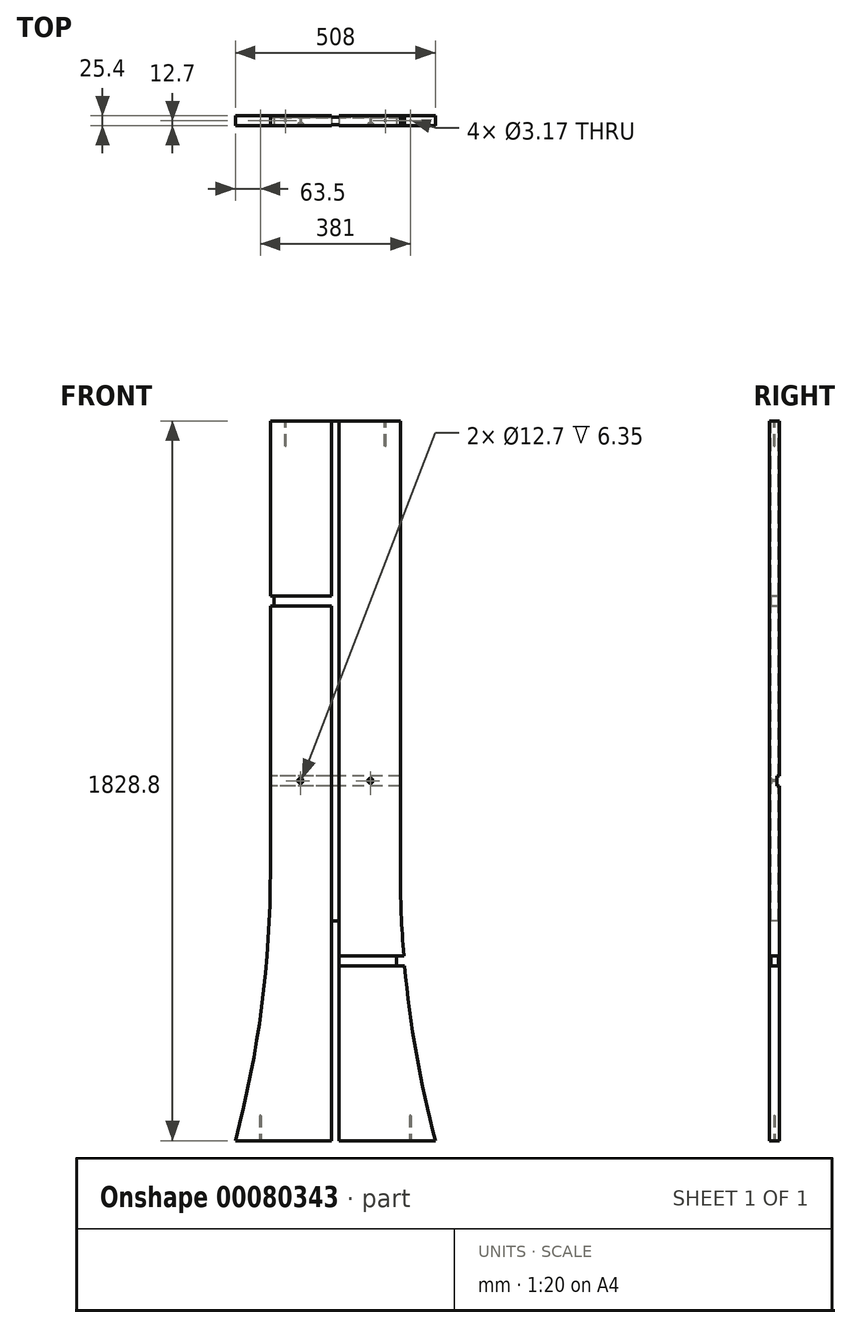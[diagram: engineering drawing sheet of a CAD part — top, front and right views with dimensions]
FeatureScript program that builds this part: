
annotation { "Feature Type Name" : "Feature", "Feature Type Description" : "" }
export const myFeature = defineFeature(function(context is Context, id is Id, definition is map)
    precondition{}
    {
        {
            var Q0;
            Q0=qCreatedBy(makeId("Front.planeOp"),FACE);
            var sketch = newSketch(context, id + "F0", { "sketchPlane" : qUnion([Q0])});
            skLineSegment(sketch, "E0", {"start": v(0, 0) * mm, "end": v(0, 1828.8) * mm, "construction": true});
            skLineSegment(sketch, "E1", {"start": v(0, 1828.8) * mm, "end": v(-165.1, 1828.8) * mm});
            skLineSegment(sketch, "E2", {"start": v(0, 0) * mm, "end": v(-254, 0) * mm});
            skLineSegment(sketch, "E3", {"start": v(-165.1, 1828.8) * mm, "end": v(-165.1, 685.8) * mm});
            skArc(sketch, "E4", {"start": v(-254, 0) * mm, "mid": v(-187.42, 340.03) * mm, "end": v(-165.1, 685.8) * mm});
            skLineSegment(sketch, "E5.MirrorCS", {"start": v(0, 1828.8) * mm, "end": v(165.1, 1828.8) * mm});
            skLineSegment(sketch, "E6.MirrorCS", {"start": v(165.1, 1828.8) * mm, "end": v(165.1, 685.8) * mm});
            skArc(sketch, "E7.MirrorCS", {"start": v(254, 0) * mm, "mid": v(187.42, 340.03) * mm, "end": v(165.1, 685.8) * mm});
            skLineSegment(sketch, "E8.MirrorCS", {"start": v(0, 0) * mm, "end": v(254, 0) * mm});
            skSolve(sketch);
        }
        {
            var Q0;
            Q0=makeQuery(id+"F0.imprint","IMPRINT",FACE,{"disambiguationData":[TD([[makeQuery(id+"F0.imprint","IMPRINT",EDGE,{"derivedFrom":sQuery(id+"F0.wireOp",EDGE,"E1")}),1.0]])]});
            extrude(context, id + "F1", {"entities" : qUnion([Q0]), "endBound" : BoundingType.SYMMETRIC, "depth" : 25.4 * mm});
        }
        {
            var Q0;
            Q0=makeQuery(id+"F1.opExtrude","CAP_FACE",FACE,{"disambiguationData":[OSD([sQuery(id+"F0.wireOp",EDGE,"E1"),sQuery(id+"F0.wireOp",EDGE,"E2"),sQuery(id+"F0.wireOp",EDGE,"E3"),sQuery(id+"F0.wireOp",EDGE,"E4"),sQuery(id+"F0.wireOp",EDGE,"E6.MirrorCS"),sQuery(id+"F0.wireOp",EDGE,"E5.MirrorCS"),sQuery(id+"F0.wireOp",EDGE,"E7.MirrorCS"),sQuery(id+"F0.wireOp",EDGE,"E8.MirrorCS")])],"isStart":false});
            var sketch = newSketch(context, id + "F28", { "sketchPlane" : qUnion([Q0])});
            skLineSegment(sketch, "E9.bottom", {"start": v(9.53, 0) * mm, "end": v(-9.52, 0) * mm});
            skLineSegment(sketch, "E9.top", {"start": v(9.53, 558.8) * mm, "end": v(-9.53, 558.8) * mm});
            skLineSegment(sketch, "E9.left", {"start": v(9.53, 0) * mm, "end": v(9.53, 558.8) * mm});
            skLineSegment(sketch, "E9.right", {"start": v(-9.52, 0) * mm, "end": v(-9.53, 558.8) * mm});
            skSolve(sketch);
        }
        {
            var Q0;
            Q0=qSketchRegion(id+"F28",true);
            extrude(context, id + "F29", {"entities" : qUnion([Q0]), "operationType" : NewBodyOperationType.REMOVE, "oppositeDirection" : true, "depth" : 25.4 * mm});
        }
        {
            var Q0;
            Q0=makeQuery(id+"F28.imprint","IMPRINT",FACE,{"disambiguationData":[TD([[makeQuery(id+"F28.imprint","IMPRINT",EDGE,{"derivedFrom":sQuery(id+"F28.wireOp",EDGE,"E9.top")}),-1.0]])]});
            var sketch = newSketch(context, id + "F2", { "sketchPlane" : qUnion([Q0])});
            skPoint(sketch, "E10", {"position": v(-88.9, 914.4) * mm});
            skPoint(sketch, "E11", {"position": v(88.9, 914.4) * mm});
            skSolve(sketch);
        }
        {
            var Q0;
            Q0=sQuery(id+"F2.wireOp",VERTEX,"E10");
            var Q1;
            Q1=sQuery(id+"F2.wireOp",VERTEX,"E11");
            var Q2;
            Q2=makeQuery(id+"F1.opExtrude","SWEPT_BODY",BODY,{"disambiguationData":[OSD([sQuery(id+"F0.wireOp",EDGE,"E1"),sQuery(id+"F0.wireOp",EDGE,"E2"),sQuery(id+"F0.wireOp",EDGE,"E3"),sQuery(id+"F0.wireOp",EDGE,"E4"),sQuery(id+"F0.wireOp",EDGE,"E6.MirrorCS"),sQuery(id+"F0.wireOp",EDGE,"E5.MirrorCS"),sQuery(id+"F0.wireOp",EDGE,"E7.MirrorCS"),sQuery(id+"F0.wireOp",EDGE,"E8.MirrorCS")])]});
            hole(context, id + "F3", {"style" : HoleStyle.C_BORE, "endStyle" : HoleEndStyle.BLIND, "holeDiameter" : 3.17 * mm, "cBoreDiameter" : 12.7 * mm, "cBoreDepth" : 6.35 * mm, "holeDepth" : 63.5 * mm, "locations" : qUnion([Q0, Q1]), "scope" : qUnion([Q2])});
        }
        {
            var Q0;
            Q0=makeQuery(id+"F1.opExtrude","SWEPT_FACE",FACE,{"disambiguationData":[OSD([sQuery(id+"F0.wireOp",EDGE,"E1"),sQuery(id+"F0.wireOp",EDGE,"E5.MirrorCS")])]});
            var sketch = newSketch(context, id + "F4", { "sketchPlane" : qUnion([Q0])});
            skPoint(sketch, "E12", {"position": v(-127, 0) * mm});
            skPoint(sketch, "E13", {"position": v(127, 0) * mm});
            skSolve(sketch);
        }
        {
            var Q0;
            Q0=sQuery(id+"F4.wireOp",VERTEX,"E12");
            var Q1;
            Q1=sQuery(id+"F4.wireOp",VERTEX,"E13");
            var Q2;
            Q2=makeQuery(id+"F1.opExtrude","SWEPT_BODY",BODY,{"disambiguationData":[OSD([sQuery(id+"F0.wireOp",EDGE,"E1"),sQuery(id+"F0.wireOp",EDGE,"E2"),sQuery(id+"F0.wireOp",EDGE,"E3"),sQuery(id+"F0.wireOp",EDGE,"E4"),sQuery(id+"F0.wireOp",EDGE,"E6.MirrorCS"),sQuery(id+"F0.wireOp",EDGE,"E5.MirrorCS"),sQuery(id+"F0.wireOp",EDGE,"E7.MirrorCS"),sQuery(id+"F0.wireOp",EDGE,"E8.MirrorCS")])]});
            hole(context, id + "F5", {"style" : HoleStyle.SIMPLE, "endStyle" : HoleEndStyle.BLIND, "holeDiameter" : 3.17 * mm, "holeDepth" : 63.5 * mm, "locations" : qUnion([Q0, Q1]), "scope" : qUnion([Q2])});
        }
        {
            var Q0;
            {var subQ0=sQuery(id+"F0.wireOp",EDGE,"E8.MirrorCS");var subQ4=sQuery(id+"F0.wireOp",EDGE,"E4");var subQ6=sQuery(id+"F0.wireOp",EDGE,"E2");Q0=makeQuery(id+"F29.boolean.opBoolean","SPLIT",FACE,{"disambiguationData":[TD([makeQuery(id+"F1.opExtrude","SWEPT_FACE",FACE,{"disambiguationData":[OSD([subQ4])]})])],"derivedFrom":makeQuery(id+"F1.opExtrude","SWEPT_FACE",FACE,{"disambiguationData":[OSD([subQ6,subQ0])]})});}
            var sketch = newSketch(context, id + "F6", { "sketchPlane" : qUnion([Q0])});
            skPoint(sketch, "E14", {"position": v(-190.5, 0) * mm});
            skPoint(sketch, "E15", {"position": v(190.5, 0) * mm});
            skSolve(sketch);
        }
        {
            var Q0;
            Q0=sQuery(id+"F6.wireOp",VERTEX,"E14");
            var Q1;
            Q1=sQuery(id+"F6.wireOp",VERTEX,"E15");
            var Q2;
            Q2=makeQuery(id+"F1.opExtrude","SWEPT_BODY",BODY,{"disambiguationData":[OSD([sQuery(id+"F0.wireOp",EDGE,"E1"),sQuery(id+"F0.wireOp",EDGE,"E2"),sQuery(id+"F0.wireOp",EDGE,"E3"),sQuery(id+"F0.wireOp",EDGE,"E4"),sQuery(id+"F0.wireOp",EDGE,"E6.MirrorCS"),sQuery(id+"F0.wireOp",EDGE,"E5.MirrorCS"),sQuery(id+"F0.wireOp",EDGE,"E7.MirrorCS"),sQuery(id+"F0.wireOp",EDGE,"E8.MirrorCS")])]});
            hole(context, id + "F7", {"style" : HoleStyle.SIMPLE, "endStyle" : HoleEndStyle.BLIND, "holeDiameter" : 3.17 * mm, "holeDepth" : 63.5 * mm, "locations" : qUnion([Q0, Q1]), "scope" : qUnion([Q2])});
        }
        {
            var Q0;
            Q0=makeQuery(id+"F1.opExtrude","CAP_FACE",FACE,{"disambiguationData":[OSD([sQuery(id+"F0.wireOp",EDGE,"E1"),sQuery(id+"F0.wireOp",EDGE,"E2"),sQuery(id+"F0.wireOp",EDGE,"E3"),sQuery(id+"F0.wireOp",EDGE,"E4"),sQuery(id+"F0.wireOp",EDGE,"E6.MirrorCS"),sQuery(id+"F0.wireOp",EDGE,"E5.MirrorCS"),sQuery(id+"F0.wireOp",EDGE,"E7.MirrorCS"),sQuery(id+"F0.wireOp",EDGE,"E8.MirrorCS")])],"isStart":true});
            var sketch = newSketch(context, id + "F8", { "sketchPlane" : qUnion([Q0])});
            skLineSegment(sketch, "E16", {"start": v(-88.9, 914.4) * mm, "end": v(88.9, 914.4) * mm, "construction": true});
            skLineSegment(sketch, "E17", {"start": v(88.9, 914.4) * mm, "end": v(165.1, 914.4) * mm, "construction": true});
            skLineSegment(sketch, "E18", {"start": v(-88.9, 914.4) * mm, "end": v(-165.1, 914.4) * mm, "construction": true});
            skLineSegment(sketch, "E19.bottom", {"start": v(-165.1, 927.1) * mm, "end": v(165.1, 927.1) * mm});
            skLineSegment(sketch, "E19.top", {"start": v(-165.1, 901.7) * mm, "end": v(165.1, 901.7) * mm});
            skLineSegment(sketch, "E19.left", {"start": v(-165.1, 927.1) * mm, "end": v(-165.1, 901.7) * mm});
            skLineSegment(sketch, "E19.right", {"start": v(165.1, 927.1) * mm, "end": v(165.1, 901.7) * mm});
            skPoint(sketch, "E19.middle", {"position": v(0, 914.4) * mm});
            skSolve(sketch);
        }
        {
            var Q0;
            Q0 = qSketchRegion(id + "F8", true);
            extrude(context, id + "F9", {"entities" : qUnion([Q0]), "operationType" : NewBodyOperationType.REMOVE, "oppositeDirection" : true, "depth" : 6.35 * mm});
        }
        {
            var Q0;
            Q0=makeQuery(id+"F28.imprint","IMPRINT",FACE,{"disambiguationData":[TD([[makeQuery(id+"F28.imprint","IMPRINT",EDGE,{"derivedFrom":sQuery(id+"F28.wireOp",EDGE,"E9.top")}),-1.0]])]});
            var sketch = newSketch(context, id + "F10", { "sketchPlane" : qUnion([Q0])});
            skLineSegment(sketch, "E20", {"start": v(0, 0) * mm, "end": v(0, 558.8) * mm, "construction": true});
            skLineSegment(sketch, "E21", {"start": v(0, 558.8) * mm, "end": v(-9.52, 558.8) * mm, "construction": true});
            skLineSegment(sketch, "E22", {"start": v(0, 558.8) * mm, "end": v(9.52, 558.8) * mm, "construction": true});
            skLineSegment(sketch, "E23.bottom", {"start": v(-9.52, 558.8) * mm, "end": v(9.52, 558.8) * mm});
            skLineSegment(sketch, "E23.top", {"start": v(-9.53, 1828.8) * mm, "end": v(9.52, 1828.8) * mm});
            skLineSegment(sketch, "E23.left", {"start": v(-9.52, 558.8) * mm, "end": v(-9.52, 1828.8) * mm});
            skLineSegment(sketch, "E23.right", {"start": v(9.52, 558.8) * mm, "end": v(9.52, 1828.8) * mm});
            skSolve(sketch);
        }
        {
            var Q0;
            Q0 = qSketchRegion(id + "F10", true);
            extrude(context, id + "F11", {"entities" : qUnion([Q0]), "operationType" : NewBodyOperationType.REMOVE, "oppositeDirection" : true, "depth" : 3.17 * mm});
        }
        {
            var Q0;
            {var subQ0=sQuery(id+"F0.wireOp",EDGE,"E6.MirrorCS");var subQ1=sQuery(id+"F0.wireOp",EDGE,"E4");var subQ2=sQuery(id+"F0.wireOp",EDGE,"E3");var subQ3=sQuery(id+"F0.wireOp",EDGE,"E8.MirrorCS");var subQ4=sQuery(id+"F0.wireOp",EDGE,"E2");var subQ5=sQuery(id+"F0.wireOp",EDGE,"E7.MirrorCS");Q0=makeQuery(id+"F9.boolean.opBoolean","SPLIT",FACE,{"disambiguationData":[TD([makeQuery(id+"F1.opExtrude","SWEPT_FACE",FACE,{"disambiguationData":[OSD([subQ1])]})])],"derivedFrom":makeQuery(id+"F1.opExtrude","CAP_FACE",FACE,{"disambiguationData":[OSD([sQuery(id+"F0.wireOp",EDGE,"E1"),subQ4,subQ2,subQ1,subQ0,sQuery(id+"F0.wireOp",EDGE,"E5.MirrorCS"),subQ5,subQ3])],"isStart":true})});}
            var sketch = newSketch(context, id + "F12", { "sketchPlane" : qUnion([Q0])});
            skLineSegment(sketch, "E24.bottom", {"start": v(-9.53, 558.8) * mm, "end": v(9.53, 558.8) * mm});
            skLineSegment(sketch, "E24.top", {"start": v(-9.53, 901.7) * mm, "end": v(9.52, 901.7) * mm});
            skLineSegment(sketch, "E24.left", {"start": v(-9.53, 558.8) * mm, "end": v(-9.53, 901.7) * mm});
            skLineSegment(sketch, "E24.right", {"start": v(9.53, 558.8) * mm, "end": v(9.53, 901.7) * mm});
            skSolve(sketch);
        }
        {
            var Q0;
            Q0 = qSketchRegion(id + "F12", true);
            extrude(context, id + "F13", {"entities" : qUnion([Q0]), "operationType" : NewBodyOperationType.REMOVE, "oppositeDirection" : true, "depth" : 3.17 * mm});
        }
        {
            var Q0;
            {var subQ0=sQuery(id+"F0.wireOp",EDGE,"E5.MirrorCS");var subQ1=sQuery(id+"F0.wireOp",EDGE,"E1");var subQ2=sQuery(id+"F0.wireOp",EDGE,"E3");var subQ3=sQuery(id+"F0.wireOp",EDGE,"E6.MirrorCS");Q0=makeQuery(id+"F9.boolean.opBoolean","SPLIT",FACE,{"disambiguationData":[TD([makeQuery(id+"F9.opExtrude","SWEPT_FACE",FACE,{"disambiguationData":[OSD([sQuery(id+"F8.wireOp",EDGE,"E19.bottom")])]})])],"derivedFrom":makeQuery(id+"F1.opExtrude","CAP_FACE",FACE,{"disambiguationData":[OSD([subQ1,sQuery(id+"F0.wireOp",EDGE,"E2"),subQ2,sQuery(id+"F0.wireOp",EDGE,"E4"),subQ3,subQ0,sQuery(id+"F0.wireOp",EDGE,"E7.MirrorCS"),sQuery(id+"F0.wireOp",EDGE,"E8.MirrorCS")])],"isStart":true})});}
            var sketch = newSketch(context, id + "F14", { "sketchPlane" : qUnion([Q0])});
            skLineSegment(sketch, "E25", {"start": v(0, 927.1) * mm, "end": v(-9.53, 927.1) * mm, "construction": true});
            skLineSegment(sketch, "E26", {"start": v(0, 927.1) * mm, "end": v(9.53, 927.1) * mm, "construction": true});
            skLineSegment(sketch, "E27.bottom", {"start": v(-9.53, 927.1) * mm, "end": v(9.53, 927.1) * mm});
            skLineSegment(sketch, "E27.top", {"start": v(-9.53, 1828.8) * mm, "end": v(9.52, 1828.8) * mm});
            skLineSegment(sketch, "E27.left", {"start": v(-9.53, 927.1) * mm, "end": v(-9.53, 1828.8) * mm});
            skLineSegment(sketch, "E27.right", {"start": v(9.52, 927.1) * mm, "end": v(9.52, 1828.8) * mm});
            skSolve(sketch);
        }
        {
            var Q0;
            Q0 = qSketchRegion(id + "F14", true);
            extrude(context, id + "F15", {"entities" : qUnion([Q0]), "operationType" : NewBodyOperationType.REMOVE, "oppositeDirection" : true, "depth" : 3.17 * mm});
        }
        {
            var Q0;
            Q0=makeQuery(id+"F28.imprint","IMPRINT",FACE,{"disambiguationData":[TD([[makeQuery(id+"F28.imprint","IMPRINT",EDGE,{"derivedFrom":sQuery(id+"F28.wireOp",EDGE,"E9.top")}),-1.0]])]});
            var sketch = newSketch(context, id + "F16", { "sketchPlane" : qUnion([Q0])});
            skLineSegment(sketch, "E28", {"start": v(0, 0) * mm, "end": v(0, 457.2) * mm, "construction": true});
            skLineSegment(sketch, "E29", {"start": v(0, 457.2) * mm, "end": v(193.68, 457.2) * mm});
            skLineSegment(sketch, "E30", {"start": v(193.68, 457.2) * mm, "end": v(193.68, 444.5) * mm});
            skLineSegment(sketch, "E31", {"start": v(0, 457.2) * mm, "end": v(0, 469.9) * mm});
            skLineSegment(sketch, "E32.bottom", {"start": v(0, 469.9) * mm, "end": v(193.68, 469.9) * mm});
            skLineSegment(sketch, "E32.top", {"start": v(0, 444.5) * mm, "end": v(193.68, 444.5) * mm});
            skLineSegment(sketch, "E32.left", {"start": v(0, 469.9) * mm, "end": v(0, 444.5) * mm});
            skLineSegment(sketch, "E32.right", {"start": v(193.68, 469.9) * mm, "end": v(193.68, 444.5) * mm});
            skSolve(sketch);
        }
        {
            var Q0;
            Q0=makeQuery(id+"F28.imprint","IMPRINT",FACE,{"disambiguationData":[TD([[makeQuery(id+"F28.imprint","IMPRINT",EDGE,{"derivedFrom":sQuery(id+"F28.wireOp",EDGE,"E9.top")}),-1.0]])]});
            var sketch = newSketch(context, id + "F17", { "sketchPlane" : qUnion([Q0])});
            skLineSegment(sketch, "E33", {"start": v(0, 0) * mm, "end": v(0, 457.2) * mm, "construction": true});
            skLineSegment(sketch, "E34", {"start": v(0, 457.2) * mm, "end": v(3.18, 457.2) * mm, "construction": true});
            skLineSegment(sketch, "E35", {"start": v(3.18, 457.2) * mm, "end": v(3.18, 444.5) * mm, "construction": true});
            skLineSegment(sketch, "E36", {"start": v(3.17, 457.2) * mm, "end": v(155.58, 457.2) * mm, "construction": true});
            skLineSegment(sketch, "E37", {"start": v(155.58, 457.2) * mm, "end": v(155.58, 469.9) * mm, "construction": true});
            skLineSegment(sketch, "E38", {"start": v(155.58, 457.2) * mm, "end": v(155.58, 444.5) * mm, "construction": true});
            skLineSegment(sketch, "E39", {"start": v(155.58, 444.5) * mm, "end": v(206.38, 444.5) * mm, "construction": true});
            skLineSegment(sketch, "E40.bottom", {"start": v(155.58, 469.9) * mm, "end": v(206.38, 469.9) * mm});
            skLineSegment(sketch, "E40.top", {"start": v(155.58, 444.5) * mm, "end": v(206.38, 444.5) * mm});
            skLineSegment(sketch, "E40.left", {"start": v(155.58, 469.9) * mm, "end": v(155.58, 444.5) * mm});
            skLineSegment(sketch, "E40.right", {"start": v(206.38, 469.9) * mm, "end": v(206.38, 444.5) * mm});
            skSolve(sketch);
        }
        {
            var Q0;
            Q0 = qSketchRegion(id + "F17", true);
            extrude(context, id + "F18", {"entities" : qUnion([Q0]), "operationType" : NewBodyOperationType.REMOVE, "oppositeDirection" : true, "depth" : 25.4 * mm});
        }
        {
            var Q0;
            Q0 = qSketchRegion(id + "F16", true);
            extrude(context, id + "F19", {"entities" : qUnion([Q0]), "operationType" : NewBodyOperationType.REMOVE, "oppositeDirection" : true, "depth" : 3.17 * mm});
        }
        {
            var Q0;
            {var subQ1=sQuery(id+"F0.wireOp",EDGE,"E7.MirrorCS");var subQ3=sQuery(id+"F0.wireOp",EDGE,"E6.MirrorCS");var subQ4=makeQuery(id+"F1.opExtrude","SWEPT_FACE",FACE,{"disambiguationData":[OSD([subQ3])]});var subQ5=sQuery(id+"F0.wireOp",EDGE,"E8.MirrorCS");var subQ6=sQuery(id+"F0.wireOp",EDGE,"E2");var subQ9=sQuery(id+"F0.wireOp",EDGE,"E4");var subQ10=sQuery(id+"F0.wireOp",EDGE,"E3");Q0=makeQuery(id+"F13.boolean.opBoolean","SPLIT",FACE,{"disambiguationData":[TD([subQ4])],"derivedFrom":makeQuery(id+"F9.boolean.opBoolean","SPLIT",FACE,{"disambiguationData":[TD([makeQuery(id+"F1.opExtrude","SWEPT_FACE",FACE,{"disambiguationData":[OSD([subQ9])]})])],"derivedFrom":makeQuery(id+"F1.opExtrude","CAP_FACE",FACE,{"disambiguationData":[OSD([sQuery(id+"F0.wireOp",EDGE,"E1"),subQ6,subQ10,subQ9,subQ3,sQuery(id+"F0.wireOp",EDGE,"E5.MirrorCS"),subQ1,subQ5])],"isStart":true})})});}
            var sketch = newSketch(context, id + "F20", { "sketchPlane" : qUnion([Q0])});
            skLineSegment(sketch, "E41", {"start": v(0, 0) * mm, "end": v(0, 457.2) * mm, "construction": true});
            skLineSegment(sketch, "E42", {"start": v(0, 457.2) * mm, "end": v(-203.2, 457.2) * mm, "construction": true});
            skPoint(sketch, "E42.endSnap0", {"position": v(-155.58, 457.2) * mm});
            skLineSegment(sketch, "E43.bottom", {"start": v(-203.2, 444.5) * mm, "end": v(0, 444.5) * mm});
            skLineSegment(sketch, "E43.top", {"start": v(-203.2, 469.9) * mm, "end": v(0, 469.9) * mm});
            skLineSegment(sketch, "E43.left", {"start": v(-203.2, 444.5) * mm, "end": v(-203.2, 469.9) * mm});
            skLineSegment(sketch, "E43.right", {"start": v(0, 444.5) * mm, "end": v(0, 469.9) * mm});
            skPoint(sketch, "E43.middle", {"position": v(-101.6, 457.2) * mm});
            skSolve(sketch);
        }
        {
            var Q0;
            Q0 = qSketchRegion(id + "F20", true);
            extrude(context, id + "F21", {"entities" : qUnion([Q0]), "operationType" : NewBodyOperationType.REMOVE, "oppositeDirection" : true, "depth" : 3.17 * mm});
        }
        {
            var Q0;
            Q0=makeQuery(id+"F28.imprint","IMPRINT",FACE,{"disambiguationData":[TD([[makeQuery(id+"F28.imprint","IMPRINT",EDGE,{"derivedFrom":sQuery(id+"F28.wireOp",EDGE,"E9.top")}),-1.0]])]});
            var sketch = newSketch(context, id + "F22", { "sketchPlane" : qUnion([Q0])});
            skLineSegment(sketch, "E44", {"start": v(0, 0) * mm, "end": v(0, 1371.6) * mm, "construction": true});
            skLineSegment(sketch, "E45", {"start": v(0, 1371.6) * mm, "end": v(-165.1, 1371.6) * mm, "construction": true});
            skLineSegment(sketch, "E46.bottom", {"start": v(-174.63, 1358.9) * mm, "end": v(-155.58, 1358.9) * mm});
            skLineSegment(sketch, "E46.top", {"start": v(-174.63, 1384.3) * mm, "end": v(-155.58, 1384.3) * mm});
            skLineSegment(sketch, "E46.left", {"start": v(-174.63, 1358.9) * mm, "end": v(-174.63, 1384.3) * mm});
            skLineSegment(sketch, "E46.right", {"start": v(-155.58, 1358.9) * mm, "end": v(-155.58, 1384.3) * mm});
            skPoint(sketch, "E46.middle", {"position": v(-165.1, 1371.6) * mm});
            skSolve(sketch);
        }
        {
            var Q0;
            Q0 = qSketchRegion(id + "F22", true);
            extrude(context, id + "F23", {"entities" : qUnion([Q0]), "operationType" : NewBodyOperationType.REMOVE, "oppositeDirection" : true, "depth" : 25.4 * mm});
        }
        {
            var Q0;
            Q0=makeQuery(id+"F28.imprint","IMPRINT",FACE,{"disambiguationData":[TD([[makeQuery(id+"F28.imprint","IMPRINT",EDGE,{"derivedFrom":sQuery(id+"F28.wireOp",EDGE,"E9.top")}),-1.0]])]});
            var sketch = newSketch(context, id + "F24", { "sketchPlane" : qUnion([Q0])});
            skLineSegment(sketch, "E47", {"start": v(0, 0) * mm, "end": v(0, 1371.6) * mm, "construction": true});
            skLineSegment(sketch, "E48", {"start": v(0, 1371.6) * mm, "end": v(-165.1, 1371.6) * mm, "construction": true});
            skLineSegment(sketch, "E49", {"start": v(-165.1, 1371.6) * mm, "end": v(-165.1, 1358.9) * mm, "construction": true});
            skLineSegment(sketch, "E50", {"start": v(0, 1371.6) * mm, "end": v(0, 1384.3) * mm, "construction": true});
            skLineSegment(sketch, "E51", {"start": v(0, 1384.3) * mm, "end": v(-6.35, 1384.3) * mm, "construction": true});
            skLineSegment(sketch, "E52.bottom", {"start": v(-165.1, 1358.9) * mm, "end": v(-6.35, 1358.9) * mm});
            skLineSegment(sketch, "E52.top", {"start": v(-165.1, 1384.3) * mm, "end": v(-6.35, 1384.3) * mm});
            skLineSegment(sketch, "E52.left", {"start": v(-165.1, 1358.9) * mm, "end": v(-165.1, 1384.3) * mm});
            skLineSegment(sketch, "E52.right", {"start": v(-6.35, 1358.9) * mm, "end": v(-6.35, 1384.3) * mm});
            skSolve(sketch);
        }
        {
            var Q0;
            Q0 = qSketchRegion(id + "F24", true);
            extrude(context, id + "F25", {"entities" : qUnion([Q0]), "operationType" : NewBodyOperationType.REMOVE, "oppositeDirection" : true, "depth" : 3.17 * mm});
        }
        {
            var Q0;
            {var subQ0=sQuery(id+"F0.wireOp",EDGE,"E5.MirrorCS");var subQ1=sQuery(id+"F0.wireOp",EDGE,"E1");var subQ3=sQuery(id+"F0.wireOp",EDGE,"E3");var subQ4=makeQuery(id+"F1.opExtrude","SWEPT_FACE",FACE,{"disambiguationData":[OSD([subQ3])]});var subQ5=makeQuery(id+"F9.opExtrude","SWEPT_FACE",FACE,{"disambiguationData":[OSD([sQuery(id+"F8.wireOp",EDGE,"E19.bottom")])]});var subQ6=sQuery(id+"F0.wireOp",EDGE,"E6.MirrorCS");Q0=makeQuery(id+"F15.boolean.opBoolean","SPLIT",FACE,{"disambiguationData":[TD([subQ4])],"derivedFrom":makeQuery(id+"F9.boolean.opBoolean","SPLIT",FACE,{"disambiguationData":[TD([subQ5])],"derivedFrom":makeQuery(id+"F1.opExtrude","CAP_FACE",FACE,{"disambiguationData":[OSD([subQ1,sQuery(id+"F0.wireOp",EDGE,"E2"),subQ3,sQuery(id+"F0.wireOp",EDGE,"E4"),subQ6,subQ0,sQuery(id+"F0.wireOp",EDGE,"E7.MirrorCS"),sQuery(id+"F0.wireOp",EDGE,"E8.MirrorCS")])],"isStart":true})})});}
            var sketch = newSketch(context, id + "F26", { "sketchPlane" : qUnion([Q0])});
            skLineSegment(sketch, "E53", {"start": v(0, 0) * mm, "end": v(0, 1371.6) * mm, "construction": true});
            skLineSegment(sketch, "E54", {"start": v(0, 1371.6) * mm, "end": v(0, 1384.3) * mm, "construction": true});
            skLineSegment(sketch, "E55", {"start": v(0, 1384.3) * mm, "end": v(6.35, 1384.3) * mm, "construction": true});
            skLineSegment(sketch, "E56", {"start": v(0, 1371.6) * mm, "end": v(165.1, 1371.6) * mm, "construction": true});
            skLineSegment(sketch, "E57", {"start": v(165.1, 1371.6) * mm, "end": v(165.1, 1358.9) * mm, "construction": true});
            skLineSegment(sketch, "E58.bottom", {"start": v(6.35, 1384.3) * mm, "end": v(165.1, 1384.3) * mm});
            skLineSegment(sketch, "E58.top", {"start": v(6.35, 1358.9) * mm, "end": v(165.1, 1358.9) * mm});
            skLineSegment(sketch, "E58.left", {"start": v(6.35, 1384.3) * mm, "end": v(6.35, 1358.9) * mm});
            skLineSegment(sketch, "E58.right", {"start": v(165.1, 1384.3) * mm, "end": v(165.1, 1358.9) * mm});
            skSolve(sketch);
        }
        {
            var Q0;
            Q0 = qSketchRegion(id + "F26", true);
            extrude(context, id + "F27", {"entities" : qUnion([Q0]), "operationType" : NewBodyOperationType.REMOVE, "oppositeDirection" : true, "depth" : 3.17 * mm});
        }
    });
